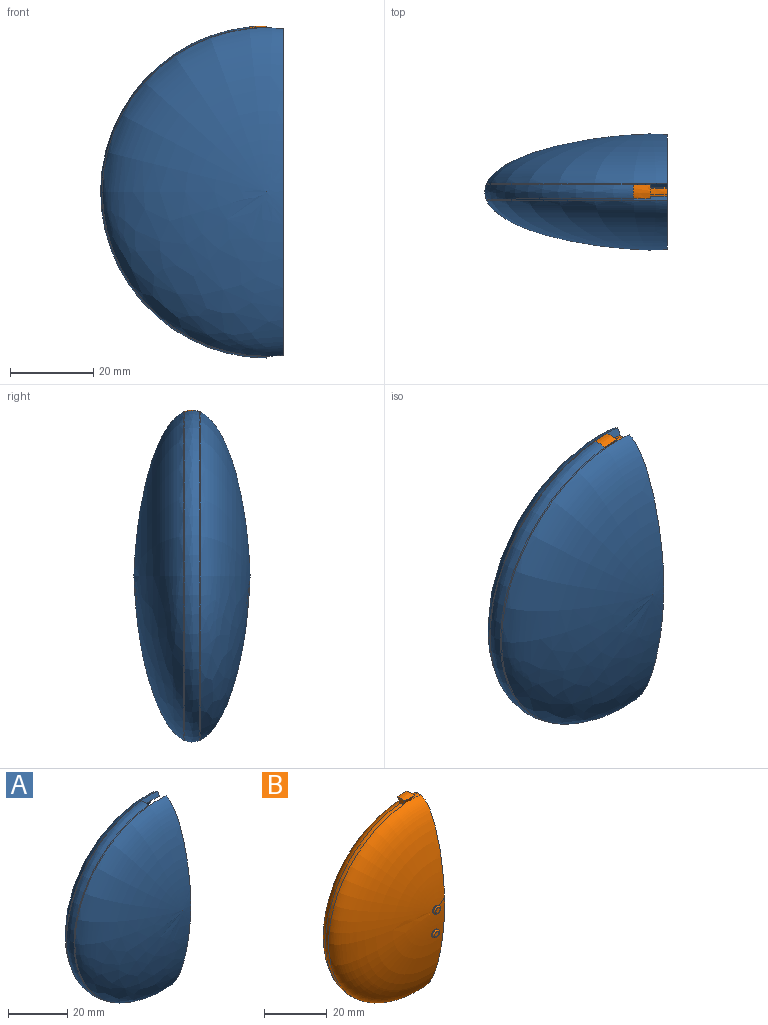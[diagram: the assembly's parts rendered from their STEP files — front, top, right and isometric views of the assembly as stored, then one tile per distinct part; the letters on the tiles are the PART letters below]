
ASSEMBLY  parts=2 mates=1
PART A: 36 faces, bbox 79.5x28x80 mm
  f0: plane 78.68x12.7mm, normal (1,0,0), area 151.5mm2, adj f9,f11,f31,f34
  f1: revolved ~79.1x39.63mm, area 36.2mm2, adj f2,f10,f32,f35
  f2: revolved ~79.78x39.96mm, area 428.8mm2, adj f1,f3,f32,f35
  f3: revolved ~79.1x39.63mm, area 36.2mm2, adj f2,f11,f32,f35
  f4: revolved ~75.79x37.97mm, area 188.6mm2, adj f5,f6,f32,f35
  f5: revolved ~75.6x37.87mm, area 35.3mm2, adj f4,f8,f32,f35
  f6: revolved ~75.6x37.87mm, area 35.3mm2, adj f4,f9,f32,f35
  f7: plane 78.68x12.7mm, normal (1,0,0), area 151.6mm2, adj f8,f10,f30,f33
  f8: revolved ~75.64x75.64mm, area 2760.8mm2, adj f5,f7,f16,f18,f21,f22,f28,f30
  f9: revolved ~75.64x75.64mm, area 2760.3mm2, adj f0,f6,f13,f15,f23,f24,f27,f31
  f10: revolved ~79.09x79.09mm, area 3121.7mm2, adj f1,f7,f30,f33
  f11: revolved ~79.09x79.09mm, area 3121.7mm2, adj f0,f3,f31,f34
  f12: plane 3x3mm, normal (0,1,0), area 7.1mm2, adj f13
  f13: cylinder r=1.5mm len=3mm, axis (0,-1,0), area 4.1mm2, adj f9,f12,f23,f24,f25
  f14: plane 3x3mm, normal (0,1,0), area 7.1mm2, adj f15
  f15: cylinder r=1.5mm len=3mm, axis (0,-1,0), area 4.1mm2, adj f9,f14,f23,f24,f25
  f16: cylinder r=1.5mm len=3mm, axis (0,-1,0), area 4.1mm2, adj f8,f17,f20,f21,f22
  f17: plane 3x3mm, normal (0,-1,0), area 7.1mm2, adj f16
  f18: cylinder r=1.5mm len=3mm, axis (0,-1,0), area 4.1mm2, adj f8,f19,f20,f21,f22
  f19: plane 3x3mm, normal (0,-1,0), area 7.1mm2, adj f18
  f20: plane 22.11x11.05mm, normal (0,-1,0), area 83mm2, adj f16,f18,f21,f22
  f21: cylinder r=8.05mm len=16.11mm, axis (0,-1,0), area 5.8mm2, adj f8,f16,f18,f20
  f22: cylinder r=11.05mm len=22.11mm, axis (0,-1,0), area 18.4mm2, adj f8,f16,f18,f20
  f23: cylinder r=11.05mm len=22.11mm, axis (0,-1,0), area 18.4mm2, adj f9,f13,f15,f25
  f24: cylinder r=8.05mm len=16.11mm, axis (0,-1,0), area 5.8mm2, adj f9,f13,f15,f25
  f25: plane 22.11x11.05mm, normal (0,1,0), area 83mm2, adj f13,f15,f23,f24
  f26: plane 3x3mm, normal (0,1,0), area 7.1mm2, adj f27
  f27: cylinder r=1.5mm len=3mm, axis (0,1,0), area 5.2mm2, adj f9,f26
  f28: cylinder r=1.5mm len=3mm, axis (0,1,0), area 5.2mm2, adj f8,f29
  f29: plane 3x3mm, normal (0,-1,0), area 7.1mm2, adj f28
  f30: cone r=37.82mm half-angle=62.5deg, axis (0,1,0), area 15.7mm2, adj f7,f8,f10,f32
  f31: cone r=37.82mm half-angle=62.5deg, axis (0,-1,0), area 15.7mm2, adj f0,f9,f11,f32
  f32: plane 4.01x2.29mm, normal (0.99,0,0.1), area 6.3mm2, adj f1,f2,f3,f4,f5,f6,f30,f31
  f33: cone r=37.82mm half-angle=62.5deg, axis (0,1,0), area 7.8mm2, adj f7,f8,f10,f35
  f34: cone r=37.82mm half-angle=62.5deg, axis (0,-1,0), area 7.8mm2, adj f0,f9,f11,f35
  f35: plane 4.01x2.31mm, normal (1,0,0), area 6.3mm2, adj f1,f2,f3,f4,f5,f6,f33,f34
PART B: 23 faces, bbox 75.3x25x77.8 mm
  f0: revolved ~4.01x1.34mm, area 5.4mm2, adj f1,f13,f14,f21
  f1: revolved ~75.26x75.26mm, area 2852.8mm2, adj f0,f2,f5,f9,f10,f21
  f2: cylinder r=1.5mm len=3mm, axis (0,-1,0), area 4mm2, adj f1,f3
  f3: torus R=1mm, axis (0,-1,0), area 6.5mm2, adj f2,f4
  f4: plane 2x2mm, normal (0,1,0), area 3.1mm2, adj f3
  f5: cone r=37.63mm half-angle=62.5deg, axis (0,1,0), area 9.3mm2, adj f1,f6,f8,f13
  f6: revolved ~4.18x3.45mm, area 14.8mm2, adj f5,f7,f8,f13
  f7: cone r=37.63mm half-angle=62.5deg, axis (0,-1,0), area 9.3mm2, adj f6,f8,f13,f14
  f8: plane 3.45x2.48mm, normal (-0.99,0,-0.1), area 5.6mm2, adj f5,f6,f7,f9
  f9: revolved ~75.19x41.71mm, area 159.5mm2, adj f1,f8,f14,f21
  f10: cylinder r=1.5mm len=3mm, axis (0,-1,0), area 3.3mm2, adj f1,f11
  f11: torus R=1mm, axis (0,-1,0), area 6.5mm2, adj f10,f12
  f12: plane 2x2mm, normal (0,1,0), area 3.1mm2, adj f11
  f13: plane 3.45x2.5mm, normal (1,0,0), area 5.6mm2, adj f0,f5,f6,f7
  f14: revolved ~75.26x74.24mm, area -7945.3mm2, adj f0,f7,f9,f15,f18,f21
  f15: cylinder r=1.5mm len=3mm, axis (0,1,0), area 4mm2, adj f14,f16
  f16: torus R=1mm, axis (0,-1,0), area 6.5mm2, adj f15,f17
  f17: plane 2x2mm, normal (0,1,0), area 3.1mm2, adj f16
  f18: cylinder r=1.5mm len=3mm, axis (0,1,0), area 3.3mm2, adj f14,f19
  f19: torus R=1mm, axis (0,-1,0), area 6.5mm2, adj f18,f20
  f20: plane 2x2mm, normal (0,-1,0), area 3.1mm2, adj f19
  f21: plane 74.99x23.06mm, normal (1,0,0), area 278.7mm2, adj f0,f1,f9,f14,f22
  f22: revolved ~71.4x71.4mm, area 5179.4mm2, adj f21
PLACE A at identity fixed
PLACE B rot(axis=(0,1,0),0deg) t=(0,0,0)mm
MATE revolute A.f27 <-> B.f10  axis (0,-1,0) through (0,12.5,0)mm
